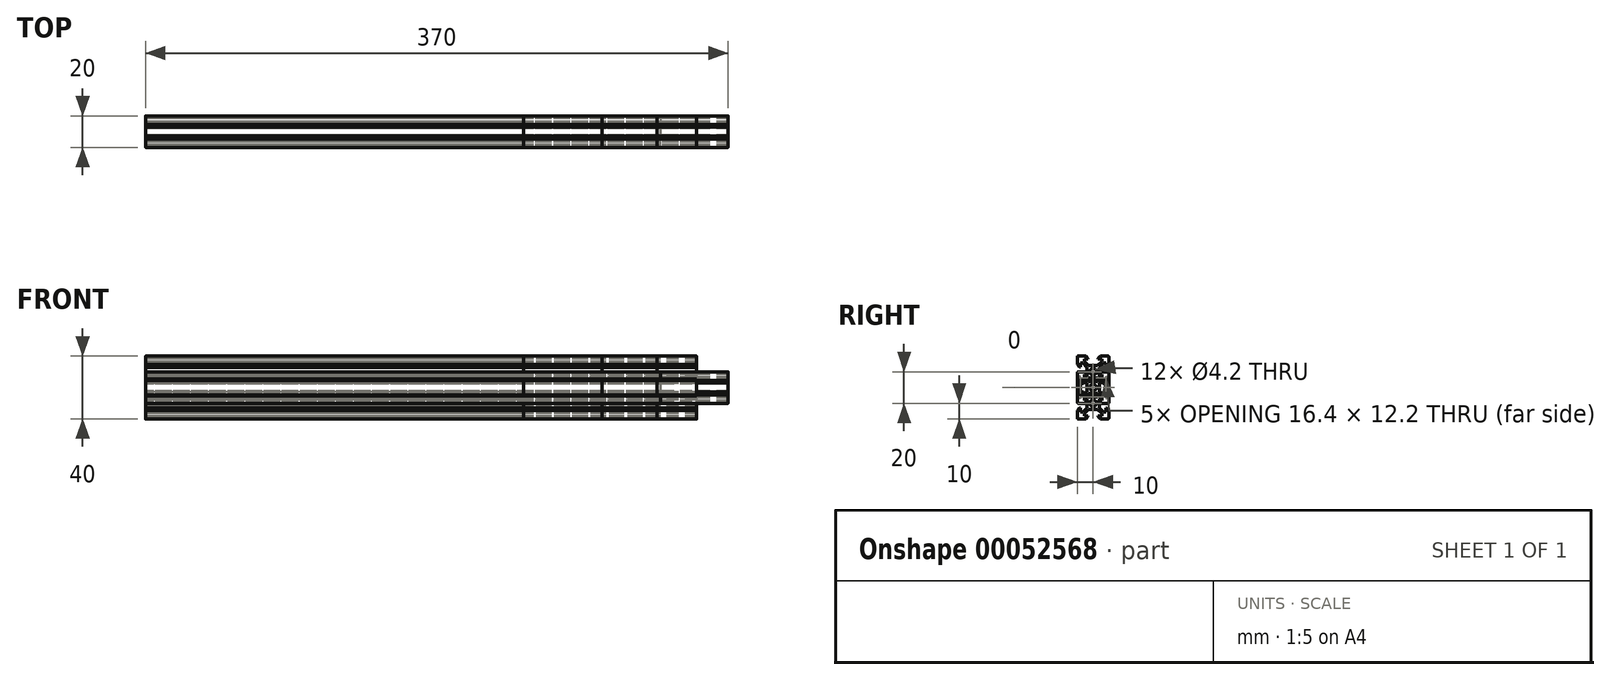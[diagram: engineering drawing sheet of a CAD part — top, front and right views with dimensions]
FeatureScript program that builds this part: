
annotation { "Feature Type Name" : "Feature", "Feature Type Description" : "" }
export const myFeature = defineFeature(function(context is Context, id is Id, definition is map)
    precondition{}
    {
        {
            var Q0;
            Q0=qCreatedBy(makeId("Right.planeOp"),FACE);
            var sketch = newSketch(context, id + "F0", { "sketchPlane" : qUnion([Q0])});
            skLineSegment(sketch, "E0", {"start": v(0, 13.9) * mm, "end": v(-2.84, 13.9) * mm});
            skLineSegment(sketch, "E1", {"start": v(-2.84, 13.9) * mm, "end": v(-5.5, 16.56) * mm});
            skLineSegment(sketch, "E2", {"start": v(-5.5, 16.56) * mm, "end": v(-5.5, 18.2) * mm});
            skLineSegment(sketch, "E3", {"start": v(-5.5, 18.2) * mm, "end": v(-3.13, 18.2) * mm});
            skLineSegment(sketch, "E4", {"start": v(-3.13, 18.2) * mm, "end": v(-3.13, 18.55) * mm});
            skLineSegment(sketch, "E5", {"start": v(-3.13, 18.55) * mm, "end": v(-4.58, 20) * mm});
            skLineSegment(sketch, "E6", {"start": v(-4.58, 20) * mm, "end": v(-9.5, 20) * mm});
            skLineSegment(sketch, "E7", {"start": v(-10, 20) * mm, "end": v(0, 10) * mm, "construction": true});
            skLineSegment(sketch, "E8.MirrorCS", {"start": v(-3.9, 10) * mm, "end": v(-3.9, 12.84) * mm});
            skLineSegment(sketch, "E9.MirrorCS", {"start": v(-3.9, 12.84) * mm, "end": v(-6.56, 15.5) * mm});
            skLineSegment(sketch, "E10.MirrorCS", {"start": v(-6.56, 15.5) * mm, "end": v(-8.2, 15.5) * mm});
            skLineSegment(sketch, "E11.MirrorCS", {"start": v(-8.2, 15.5) * mm, "end": v(-8.2, 13.13) * mm});
            skLineSegment(sketch, "E12.MirrorCS", {"start": v(-8.2, 13.12) * mm, "end": v(-8.55, 13.12) * mm});
            skLineSegment(sketch, "E13.MirrorCS", {"start": v(-8.55, 13.13) * mm, "end": v(-10, 14.58) * mm});
            skLineSegment(sketch, "E14.MirrorCS", {"start": v(-10, 14.58) * mm, "end": v(-10, 19.5) * mm});
            skCircle(sketch, "E15", {"center": v(0, 10) * mm, "radius": 2.1 * mm});
            skPoint(sketch, "E16.visualSharp", {"position": v(-10, 20) * mm});
            skArc(sketch, "E16.filletArc", {"start": v(-9.5, 20) * mm, "mid": v(-9.85, 19.85) * mm, "end": v(-10, 19.5) * mm});
            skLineSegment(sketch, "E17", {"start": v(0, 10) * mm, "end": v(-3.9, 10) * mm, "construction": true});
            skLineSegment(sketch, "E18.MirrorCS", {"start": v(-3.9, 10) * mm, "end": v(-3.9, 7.16) * mm});
            skLineSegment(sketch, "E19.MirrorCS", {"start": v(0, 6.1) * mm, "end": v(-2.84, 6.1) * mm});
            skLineSegment(sketch, "E20.MirrorCS", {"start": v(-3.9, 7.16) * mm, "end": v(-6.56, 4.5) * mm});
            skLineSegment(sketch, "E21.MirrorCS", {"start": v(-6.56, 4.5) * mm, "end": v(-8.2, 4.5) * mm});
            skLineSegment(sketch, "E22.MirrorCS", {"start": v(-8.2, 4.5) * mm, "end": v(-8.2, 6.87) * mm});
            skLineSegment(sketch, "E23.MirrorCS", {"start": v(-8.2, 6.87) * mm, "end": v(-8.55, 6.87) * mm});
            skLineSegment(sketch, "E24.MirrorCS", {"start": v(-8.55, 6.87) * mm, "end": v(-10, 5.42) * mm});
            skLineSegment(sketch, "E25", {"start": v(-10, 5.42) * mm, "end": v(-10, 0) * mm});
            skLineSegment(sketch, "E26", {"start": v(-2.84, 6.1) * mm, "end": v(-6.24, 2.7) * mm});
            skLineSegment(sketch, "E27", {"start": v(-6.24, 2.7) * mm, "end": v(-8.2, 2.7) * mm});
            skLineSegment(sketch, "E28", {"start": v(-8.2, 2.7) * mm, "end": v(-8.2, 0) * mm});
            skLineSegment(sketch, "E29.MirrorCS", {"start": v(0, 13.9) * mm, "end": v(2.84, 13.9) * mm});
            skLineSegment(sketch, "E30.MirrorCS", {"start": v(2.84, 13.9) * mm, "end": v(5.5, 16.56) * mm});
            skLineSegment(sketch, "E31.MirrorCS", {"start": v(5.5, 16.56) * mm, "end": v(5.5, 18.2) * mm});
            skLineSegment(sketch, "E32.MirrorCS", {"start": v(5.5, 18.2) * mm, "end": v(3.13, 18.2) * mm});
            skLineSegment(sketch, "E33.MirrorCS", {"start": v(3.13, 18.2) * mm, "end": v(3.13, 18.55) * mm});
            skLineSegment(sketch, "E34.MirrorCS", {"start": v(3.13, 18.55) * mm, "end": v(4.58, 20) * mm});
            skLineSegment(sketch, "E35.MirrorCS", {"start": v(4.58, 20) * mm, "end": v(9.5, 20) * mm});
            skArc(sketch, "E36.MirrorCS", {"start": v(9.5, 20) * mm, "mid": v(9.85, 19.85) * mm, "end": v(10, 19.5) * mm});
            skLineSegment(sketch, "E37.MirrorCS", {"start": v(10, 14.58) * mm, "end": v(10, 19.5) * mm});
            skLineSegment(sketch, "E38.MirrorCS", {"start": v(8.55, 13.13) * mm, "end": v(10, 14.58) * mm});
            skLineSegment(sketch, "E39.MirrorCS", {"start": v(8.2, 13.12) * mm, "end": v(8.55, 13.12) * mm});
            skLineSegment(sketch, "E40.MirrorCS", {"start": v(8.2, 15.5) * mm, "end": v(8.2, 13.13) * mm});
            skLineSegment(sketch, "E41.MirrorCS", {"start": v(6.56, 15.5) * mm, "end": v(8.2, 15.5) * mm});
            skLineSegment(sketch, "E42.MirrorCS", {"start": v(3.9, 12.84) * mm, "end": v(6.56, 15.5) * mm});
            skLineSegment(sketch, "E43.MirrorCS", {"start": v(3.9, 10) * mm, "end": v(3.9, 12.84) * mm});
            skLineSegment(sketch, "E44.MirrorCS", {"start": v(3.9, 10) * mm, "end": v(3.9, 7.16) * mm});
            skLineSegment(sketch, "E45.MirrorCS", {"start": v(3.9, 7.16) * mm, "end": v(6.56, 4.5) * mm});
            skLineSegment(sketch, "E46.MirrorCS", {"start": v(6.56, 4.5) * mm, "end": v(8.2, 4.5) * mm});
            skLineSegment(sketch, "E47.MirrorCS", {"start": v(8.2, 4.5) * mm, "end": v(8.2, 6.87) * mm});
            skLineSegment(sketch, "E48.MirrorCS", {"start": v(8.2, 6.87) * mm, "end": v(8.55, 6.87) * mm});
            skLineSegment(sketch, "E49.MirrorCS", {"start": v(8.55, 6.87) * mm, "end": v(10, 5.42) * mm});
            skLineSegment(sketch, "E50.MirrorCS", {"start": v(10, 5.42) * mm, "end": v(10, 0) * mm});
            skLineSegment(sketch, "E51.MirrorCS", {"start": v(0, 6.1) * mm, "end": v(2.84, 6.1) * mm});
            skLineSegment(sketch, "E52.MirrorCS", {"start": v(2.84, 6.1) * mm, "end": v(6.24, 2.7) * mm});
            skLineSegment(sketch, "E53.MirrorCS", {"start": v(6.24, 2.7) * mm, "end": v(8.2, 2.7) * mm});
            skLineSegment(sketch, "E54.MirrorCS", {"start": v(8.2, 2.7) * mm, "end": v(8.2, 0) * mm});
            skLineSegment(sketch, "E55.MirrorCS", {"start": v(8.2, -2.7) * mm, "end": v(8.2, 0) * mm});
            skLineSegment(sketch, "E56.MirrorCS", {"start": v(6.24, -2.7) * mm, "end": v(8.2, -2.7) * mm});
            skLineSegment(sketch, "E57.MirrorCS", {"start": v(2.84, -6.1) * mm, "end": v(6.24, -2.7) * mm});
            skLineSegment(sketch, "E58.MirrorCS", {"start": v(0, -6.1) * mm, "end": v(2.84, -6.1) * mm});
            skLineSegment(sketch, "E59.MirrorCS", {"start": v(0, -6.1) * mm, "end": v(-2.84, -6.1) * mm});
            skLineSegment(sketch, "E60.MirrorCS", {"start": v(-2.84, -6.1) * mm, "end": v(-6.24, -2.7) * mm});
            skLineSegment(sketch, "E61.MirrorCS", {"start": v(-6.24, -2.7) * mm, "end": v(-8.2, -2.7) * mm});
            skLineSegment(sketch, "E62.MirrorCS", {"start": v(-8.2, -2.7) * mm, "end": v(-8.2, 0) * mm});
            skLineSegment(sketch, "E63.MirrorCS", {"start": v(10, -5.42) * mm, "end": v(10, 0) * mm});
            skLineSegment(sketch, "E64.MirrorCS", {"start": v(8.55, -6.87) * mm, "end": v(10, -5.42) * mm});
            skLineSegment(sketch, "E65.MirrorCS", {"start": v(8.2, -6.87) * mm, "end": v(8.55, -6.87) * mm});
            skLineSegment(sketch, "E66.MirrorCS", {"start": v(8.2, -4.5) * mm, "end": v(8.2, -6.87) * mm});
            skLineSegment(sketch, "E67.MirrorCS", {"start": v(6.56, -4.5) * mm, "end": v(8.2, -4.5) * mm});
            skLineSegment(sketch, "E68.MirrorCS", {"start": v(3.9, -7.16) * mm, "end": v(6.56, -4.5) * mm});
            skLineSegment(sketch, "E69.MirrorCS", {"start": v(3.9, -10) * mm, "end": v(3.9, -7.16) * mm});
            skLineSegment(sketch, "E70.MirrorCS", {"start": v(3.9, -10) * mm, "end": v(3.9, -12.84) * mm});
            skLineSegment(sketch, "E71.MirrorCS", {"start": v(3.9, -12.84) * mm, "end": v(6.56, -15.5) * mm});
            skLineSegment(sketch, "E72.MirrorCS", {"start": v(6.56, -15.5) * mm, "end": v(8.2, -15.5) * mm});
            skLineSegment(sketch, "E73.MirrorCS", {"start": v(8.2, -15.5) * mm, "end": v(8.2, -13.13) * mm});
            skLineSegment(sketch, "E74.MirrorCS", {"start": v(8.2, -13.12) * mm, "end": v(8.55, -13.12) * mm});
            skLineSegment(sketch, "E75.MirrorCS", {"start": v(8.55, -13.13) * mm, "end": v(10, -14.58) * mm});
            skLineSegment(sketch, "E76.MirrorCS", {"start": v(10, -14.58) * mm, "end": v(10, -19.5) * mm});
            skArc(sketch, "E77.MirrorCS", {"start": v(9.5, -20) * mm, "mid": v(9.85, -19.85) * mm, "end": v(10, -19.5) * mm});
            skLineSegment(sketch, "E78.MirrorCS", {"start": v(4.58, -20) * mm, "end": v(9.5, -20) * mm});
            skLineSegment(sketch, "E79.MirrorCS", {"start": v(3.13, -18.55) * mm, "end": v(4.58, -20) * mm});
            skLineSegment(sketch, "E80.MirrorCS", {"start": v(3.13, -18.2) * mm, "end": v(3.13, -18.55) * mm});
            skLineSegment(sketch, "E81.MirrorCS", {"start": v(5.5, -18.2) * mm, "end": v(3.13, -18.2) * mm});
            skLineSegment(sketch, "E82.MirrorCS", {"start": v(5.5, -16.56) * mm, "end": v(5.5, -18.2) * mm});
            skLineSegment(sketch, "E83.MirrorCS", {"start": v(2.84, -13.9) * mm, "end": v(5.5, -16.56) * mm});
            skLineSegment(sketch, "E84.MirrorCS", {"start": v(0, -13.9) * mm, "end": v(2.84, -13.9) * mm});
            skLineSegment(sketch, "E85.MirrorCS", {"start": v(0, -13.9) * mm, "end": v(-2.84, -13.9) * mm});
            skLineSegment(sketch, "E86.MirrorCS", {"start": v(-2.84, -13.9) * mm, "end": v(-5.5, -16.56) * mm});
            skLineSegment(sketch, "E87.MirrorCS", {"start": v(-5.5, -16.56) * mm, "end": v(-5.5, -18.2) * mm});
            skLineSegment(sketch, "E88.MirrorCS", {"start": v(-5.5, -18.2) * mm, "end": v(-3.13, -18.2) * mm});
            skLineSegment(sketch, "E89.MirrorCS", {"start": v(-3.13, -18.2) * mm, "end": v(-3.13, -18.55) * mm});
            skLineSegment(sketch, "E90.MirrorCS", {"start": v(-3.13, -18.55) * mm, "end": v(-4.58, -20) * mm});
            skLineSegment(sketch, "E91.MirrorCS", {"start": v(-4.58, -20) * mm, "end": v(-9.5, -20) * mm});
            skArc(sketch, "E92.MirrorCS", {"start": v(-9.5, -20) * mm, "mid": v(-9.85, -19.85) * mm, "end": v(-10, -19.5) * mm});
            skLineSegment(sketch, "E93.MirrorCS", {"start": v(-10, -14.58) * mm, "end": v(-10, -19.5) * mm});
            skLineSegment(sketch, "E94.MirrorCS", {"start": v(-8.55, -13.13) * mm, "end": v(-10, -14.58) * mm});
            skLineSegment(sketch, "E95.MirrorCS", {"start": v(-8.2, -13.12) * mm, "end": v(-8.55, -13.12) * mm});
            skLineSegment(sketch, "E96.MirrorCS", {"start": v(-8.2, -15.5) * mm, "end": v(-8.2, -13.13) * mm});
            skLineSegment(sketch, "E97.MirrorCS", {"start": v(-6.56, -15.5) * mm, "end": v(-8.2, -15.5) * mm});
            skLineSegment(sketch, "E98.MirrorCS", {"start": v(-3.9, -12.84) * mm, "end": v(-6.56, -15.5) * mm});
            skLineSegment(sketch, "E99.MirrorCS", {"start": v(-3.9, -10) * mm, "end": v(-3.9, -12.84) * mm});
            skLineSegment(sketch, "E100.MirrorCS", {"start": v(-3.9, -10) * mm, "end": v(-3.9, -7.16) * mm});
            skLineSegment(sketch, "E101.MirrorCS", {"start": v(-3.9, -7.16) * mm, "end": v(-6.56, -4.5) * mm});
            skLineSegment(sketch, "E102.MirrorCS", {"start": v(-6.56, -4.5) * mm, "end": v(-8.2, -4.5) * mm});
            skLineSegment(sketch, "E103.MirrorCS", {"start": v(-8.2, -4.5) * mm, "end": v(-8.2, -6.87) * mm});
            skLineSegment(sketch, "E104.MirrorCS", {"start": v(-8.2, -6.87) * mm, "end": v(-8.55, -6.87) * mm});
            skLineSegment(sketch, "E105.MirrorCS", {"start": v(-8.55, -6.87) * mm, "end": v(-10, -5.42) * mm});
            skLineSegment(sketch, "E106.MirrorCS", {"start": v(-10, -5.42) * mm, "end": v(-10, 0) * mm});
            skCircle(sketch, "E107.MirrorC", {"center": v(0, -10) * mm, "radius": 2.1 * mm});
            skSolve(sketch);
        }
        {
            var Q0;
            Q0=qCreatedBy(makeId("Right.planeOp"),FACE);
            var sketch = newSketch(context, id + "F1", { "sketchPlane" : qUnion([Q0])});
            skLineSegment(sketch, "E108", {"start": v(0, 0) * mm, "end": v(-10, 10) * mm, "construction": true});
            skLineSegment(sketch, "E109", {"start": v(-9.5, 10) * mm, "end": v(-4.58, 10) * mm});
            skLineSegment(sketch, "E110", {"start": v(-4.58, 10) * mm, "end": v(-3.12, 8.54) * mm});
            skLineSegment(sketch, "E111", {"start": v(-3.12, 8.54) * mm, "end": v(-3.12, 8.2) * mm});
            skLineSegment(sketch, "E112", {"start": v(-3.12, 8.2) * mm, "end": v(-5.5, 8.2) * mm});
            skLineSegment(sketch, "E113", {"start": v(-5.5, 8.2) * mm, "end": v(-5.5, 6.56) * mm});
            skLineSegment(sketch, "E114", {"start": v(-5.5, 6.56) * mm, "end": v(-2.84, 3.9) * mm});
            skLineSegment(sketch, "E115", {"start": v(-2.84, 3.9) * mm, "end": v(0, 3.9) * mm});
            skLineSegment(sketch, "E116.MirrorCS", {"start": v(-10, 9.5) * mm, "end": v(-10, 4.58) * mm});
            skLineSegment(sketch, "E117.MirrorCS", {"start": v(-10, 4.58) * mm, "end": v(-8.54, 3.12) * mm});
            skLineSegment(sketch, "E118.MirrorCS", {"start": v(-8.54, 3.12) * mm, "end": v(-8.2, 3.12) * mm});
            skLineSegment(sketch, "E119.MirrorCS", {"start": v(-8.2, 3.12) * mm, "end": v(-8.2, 5.5) * mm});
            skLineSegment(sketch, "E120.MirrorCS", {"start": v(-8.2, 5.5) * mm, "end": v(-6.56, 5.5) * mm});
            skLineSegment(sketch, "E121.MirrorCS", {"start": v(-6.56, 5.5) * mm, "end": v(-3.9, 2.84) * mm});
            skLineSegment(sketch, "E122.MirrorCS", {"start": v(-3.9, 2.84) * mm, "end": v(-3.9, 0) * mm});
            skPoint(sketch, "E123.visualSharp", {"position": v(-10, 10) * mm});
            skArc(sketch, "E123.filletArc", {"start": v(-9.5, 10) * mm, "mid": v(-9.85, 9.85) * mm, "end": v(-10, 9.5) * mm});
            skLineSegment(sketch, "E124.MirrorCS", {"start": v(2.84, 3.9) * mm, "end": v(0, 3.9) * mm});
            skLineSegment(sketch, "E125.MirrorCS", {"start": v(5.5, 6.56) * mm, "end": v(2.84, 3.9) * mm});
            skLineSegment(sketch, "E126.MirrorCS", {"start": v(5.5, 8.2) * mm, "end": v(5.5, 6.56) * mm});
            skLineSegment(sketch, "E127.MirrorCS", {"start": v(3.12, 8.2) * mm, "end": v(5.5, 8.2) * mm});
            skLineSegment(sketch, "E128.MirrorCS", {"start": v(3.12, 8.54) * mm, "end": v(3.12, 8.2) * mm});
            skLineSegment(sketch, "E129.MirrorCS", {"start": v(4.58, 10) * mm, "end": v(3.12, 8.54) * mm});
            skLineSegment(sketch, "E130.MirrorCS", {"start": v(9.5, 10) * mm, "end": v(4.58, 10) * mm});
            skArc(sketch, "E131.MirrorCS", {"start": v(9.5, 10) * mm, "mid": v(9.85, 9.85) * mm, "end": v(10, 9.5) * mm});
            skLineSegment(sketch, "E132.MirrorCS", {"start": v(10, 9.5) * mm, "end": v(10, 4.58) * mm});
            skLineSegment(sketch, "E133.MirrorCS", {"start": v(10, 4.58) * mm, "end": v(8.54, 3.13) * mm});
            skLineSegment(sketch, "E134.MirrorCS", {"start": v(8.54, 3.12) * mm, "end": v(8.2, 3.12) * mm});
            skLineSegment(sketch, "E135.MirrorCS", {"start": v(8.2, 3.12) * mm, "end": v(8.2, 5.5) * mm});
            skLineSegment(sketch, "E136.MirrorCS", {"start": v(8.2, 5.5) * mm, "end": v(6.56, 5.5) * mm});
            skLineSegment(sketch, "E137.MirrorCS", {"start": v(6.56, 5.5) * mm, "end": v(3.9, 2.84) * mm});
            skLineSegment(sketch, "E138.MirrorCS", {"start": v(3.9, 2.84) * mm, "end": v(3.9, 0) * mm});
            skLineSegment(sketch, "E139.MirrorCS", {"start": v(-3.9, -2.84) * mm, "end": v(-3.9, 0) * mm});
            skLineSegment(sketch, "E140.MirrorCS", {"start": v(-6.56, -5.5) * mm, "end": v(-3.9, -2.84) * mm});
            skLineSegment(sketch, "E141.MirrorCS", {"start": v(-8.2, -5.5) * mm, "end": v(-6.56, -5.5) * mm});
            skLineSegment(sketch, "E142.MirrorCS", {"start": v(-8.2, -3.12) * mm, "end": v(-8.2, -5.5) * mm});
            skLineSegment(sketch, "E143.MirrorCS", {"start": v(-8.54, -3.12) * mm, "end": v(-8.2, -3.12) * mm});
            skLineSegment(sketch, "E144.MirrorCS", {"start": v(-10, -4.58) * mm, "end": v(-8.54, -3.13) * mm});
            skLineSegment(sketch, "E145.MirrorCS", {"start": v(-10, -9.5) * mm, "end": v(-10, -4.58) * mm});
            skArc(sketch, "E146.MirrorCS", {"start": v(-9.5, -10) * mm, "mid": v(-9.85, -9.85) * mm, "end": v(-10, -9.5) * mm});
            skLineSegment(sketch, "E147.MirrorCS", {"start": v(-9.5, -10) * mm, "end": v(-4.58, -10) * mm});
            skLineSegment(sketch, "E148.MirrorCS", {"start": v(-4.58, -10) * mm, "end": v(-3.12, -8.54) * mm});
            skLineSegment(sketch, "E149.MirrorCS", {"start": v(-3.12, -8.54) * mm, "end": v(-3.12, -8.2) * mm});
            skLineSegment(sketch, "E150.MirrorCS", {"start": v(-3.12, -8.2) * mm, "end": v(-5.5, -8.2) * mm});
            skLineSegment(sketch, "E151.MirrorCS", {"start": v(-5.5, -8.2) * mm, "end": v(-5.5, -6.56) * mm});
            skLineSegment(sketch, "E152.MirrorCS", {"start": v(-5.5, -6.56) * mm, "end": v(-2.84, -3.9) * mm});
            skLineSegment(sketch, "E153.MirrorCS", {"start": v(-2.84, -3.9) * mm, "end": v(0, -3.9) * mm});
            skLineSegment(sketch, "E154.MirrorCS", {"start": v(2.84, -3.9) * mm, "end": v(0, -3.9) * mm});
            skLineSegment(sketch, "E155.MirrorCS", {"start": v(5.5, -6.56) * mm, "end": v(2.84, -3.9) * mm});
            skLineSegment(sketch, "E156.MirrorCS", {"start": v(5.5, -8.2) * mm, "end": v(5.5, -6.56) * mm});
            skLineSegment(sketch, "E157.MirrorCS", {"start": v(3.12, -8.2) * mm, "end": v(5.5, -8.2) * mm});
            skLineSegment(sketch, "E158.MirrorCS", {"start": v(3.13, -8.54) * mm, "end": v(3.13, -8.2) * mm});
            skLineSegment(sketch, "E159.MirrorCS", {"start": v(4.58, -10) * mm, "end": v(3.12, -8.54) * mm});
            skLineSegment(sketch, "E160.MirrorCS", {"start": v(9.5, -10) * mm, "end": v(4.58, -10) * mm});
            skArc(sketch, "E161.MirrorCS", {"start": v(9.5, -10) * mm, "mid": v(9.85, -9.85) * mm, "end": v(10, -9.5) * mm});
            skLineSegment(sketch, "E162.MirrorCS", {"start": v(10, -9.5) * mm, "end": v(10, -4.58) * mm});
            skLineSegment(sketch, "E163.MirrorCS", {"start": v(10, -4.58) * mm, "end": v(8.54, -3.12) * mm});
            skLineSegment(sketch, "E164.MirrorCS", {"start": v(8.54, -3.12) * mm, "end": v(8.2, -3.12) * mm});
            skLineSegment(sketch, "E165.MirrorCS", {"start": v(8.2, -3.12) * mm, "end": v(8.2, -5.5) * mm});
            skLineSegment(sketch, "E166.MirrorCS", {"start": v(8.2, -5.5) * mm, "end": v(6.56, -5.5) * mm});
            skLineSegment(sketch, "E167.MirrorCS", {"start": v(6.56, -5.5) * mm, "end": v(3.9, -2.84) * mm});
            skLineSegment(sketch, "E168.MirrorCS", {"start": v(3.9, -2.84) * mm, "end": v(3.9, 0) * mm});
            skCircle(sketch, "E169", {"center": v(0, 0) * mm, "radius": 2.1 * mm});
            skSolve(sketch);
        }
        {
            var Q0;
            Q0=makeQuery(id+"F0.imprint","IMPRINT",FACE,{"disambiguationData":[TD([[makeQuery(id+"F0.imprint","IMPRINT",EDGE,{"derivedFrom":sQuery(id+"F0.wireOp",EDGE,"E0")}),1.0]])]});
            extrude(context, id + "F2", {"entities" : qUnion([Q0]), "depth" : 325 * mm});
        }
        {
            var Q0;
            Q0=makeQuery(id+"F0.imprint","IMPRINT",FACE,{"disambiguationData":[TD([[makeQuery(id+"F0.imprint","IMPRINT",EDGE,{"derivedFrom":sQuery(id+"F0.wireOp",EDGE,"E0")}),1.0]])]});
            extrude(context, id + "F3", {"entities" : qUnion([Q0]), "depth" : 240 * mm});
        }
        {
            var Q0;
            Q0=qSketchRegion(id+"F0",true);
            extrude(context, id + "F4", {"entities" : qUnion([Q0]), "depth" : 290 * mm});
        }
        {
            var Q0;
            Q0=qSketchRegion(id+"F1",true);
            extrude(context, id + "F5", {"entities" : qUnion([Q0]), "depth" : 327 * mm});
        }
        {
            var Q0;
            Q0=qSketchRegion(id+"F0",true);
            extrude(context, id + "F6", {"entities" : qUnion([Q0]), "depth" : 350 * mm});
        }
        {
            var Q0;
            Q0=qSketchRegion(id+"F1",true);
            extrude(context, id + "F7", {"entities" : qUnion([Q0]), "depth" : 370 * mm});
        }
        {
            var Q0;
            Q0=qSketchRegion(id+"F0",true);
            extrude(context, id + "F8", {"entities" : qUnion([Q0]), "depth" : 350 * mm});
        }
    });
